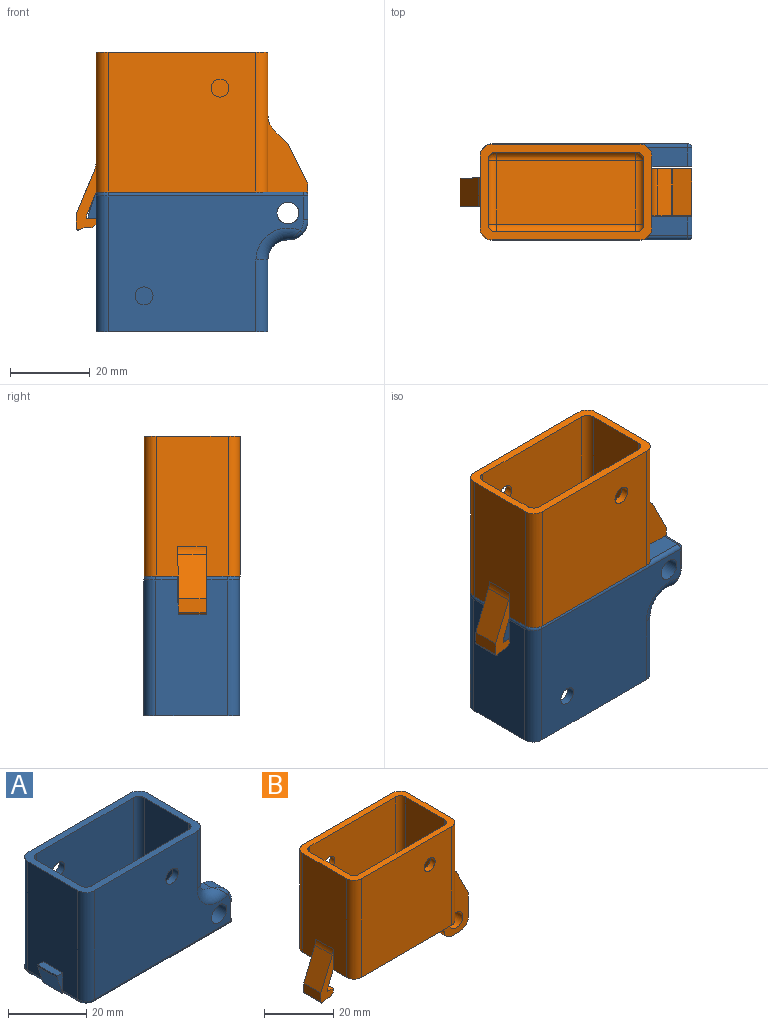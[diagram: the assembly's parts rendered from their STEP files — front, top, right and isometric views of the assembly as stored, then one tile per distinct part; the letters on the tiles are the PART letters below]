
ASSEMBLY  parts=2 mates=1
PART A: 62 faces, bbox 55.4x24.5x35 mm
  f0: plane 34x18mm, normal (-1,0,0), area 573.1mm2, adj f2,f37,f38,f39,f46,f47,f54,f61
  f1: plane 35x18mm, normal (1,0,0), area 536.5mm2, adj f2,f5,f15,f17,f22,f24,f42,f44
  f2: plane 43x24mm, normal (0,0,1), area 247.7mm2, adj f0,f1,f3,f4,f6,f7,f8,f9
  f3: plane 49x34mm, normal (0,1,0), area 1328.5mm2, adj f2,f19,f27,f42,f43,f46,f49,f50
  f4: plane 49x34mm, normal (0,-1,0), area 1328.5mm2, adj f2,f20,f28,f44,f45,f47,f56,f57
  f5: plane 52x22mm, normal (0,0,-1), area 1014.8mm2, adj f1,f15,f17,f25,f26,f37,f39,f41
  f6: plane 35x31mm, normal (0,-1,0), area 1069.1mm2, adj f2,f12,f14,f27,f31
  f7: plane 31x16mm, normal (1,0,0), area 496mm2, adj f2,f13,f14,f30
  f8: plane 35x31mm, normal (0,1,0), area 1069.1mm2, adj f2,f11,f13,f28,f34
  f9: plane 31x16mm, normal (-1,0,0), area 496mm2, adj f2,f11,f12,f35
  f10: plane 35x16mm, normal (0,0,1), area 560mm2, adj f30,f31,f34,f35
  f11: cylinder r=2mm len=31mm, axis (0,0,-1), area 97.4mm2, adj f2,f8,f9,f36
  f12: cylinder r=2mm len=31mm, axis (0,0,1), area 97.4mm2, adj f2,f6,f9,f33
  f13: cylinder r=2mm len=31mm, axis (0,0,1), area 97.4mm2, adj f2,f7,f8,f32
  f14: cylinder r=2mm len=31mm, axis (0,0,-1), area 97.4mm2, adj f2,f6,f7,f29
  f15: plane 17x10mm, normal (0,1,0), area 96mm2, adj f1,f5,f16,f20,f21,f22,f25
  f16: plane 6x4.75mm, normal (1,0,0), area 28.5mm2, adj f15,f21,f25,f57
  f17: plane 17x10mm, normal (0,-1,0), area 96mm2, adj f1,f5,f18,f19,f23,f24,f26
  f18: plane 6x4.75mm, normal (1,0,0), area 28.5mm2, adj f17,f23,f26,f50
  f19: cylinder r=2.75mm len=5.75mm, axis (0,1,0), area 99.4mm2, adj f3,f17
  f20: cylinder r=2.75mm len=5.75mm, axis (0,1,0), area 99.4mm2, adj f4,f15
  f21: cylinder r=5mm len=5mm, axis (0,1,0), area 34.2mm2, adj f15,f16,f22,f55,f56
  f22: cylinder r=5mm len=5mm, axis (0,-1,0), area 21.6mm2, adj f1,f15,f21,f45
  f23: cylinder r=5mm len=5mm, axis (0,1,0), area 34.2mm2, adj f17,f18,f24,f48,f49
  f24: cylinder r=5mm len=5mm, axis (0,-1,0), area 21.6mm2, adj f1,f17,f23,f43
  f25: cylinder r=1mm len=4.75mm, axis (0,1,0), area 7.5mm2, adj f5,f15,f16,f58
  f26: cylinder r=1mm len=4.75mm, axis (0,1,0), area 7.5mm2, adj f5,f17,f18,f51
  f27: cylinder r=2.25mm len=4.5mm, axis (0,1,0), area 28.3mm2, adj f3,f6
  f28: cylinder r=2.25mm len=4.5mm, axis (0,-1,0), area 28.3mm2, adj f4,f8
  f29: sphere r=2mm, area 6.3mm2, adj f14,f30,f31
  f30: cylinder r=2mm len=16mm, axis (0,1,0), area 50.3mm2, adj f7,f10,f29,f32
  f31: cylinder r=2mm len=35mm, axis (1,0,0), area 110mm2, adj f6,f10,f29,f33
  f32: sphere r=2mm, area 6.3mm2, adj f13,f30,f34
  f33: sphere r=2mm, area 6.3mm2, adj f12,f31,f35
  f34: cylinder r=2mm len=35mm, axis (-1,0,0), area 110mm2, adj f8,f10,f32,f36
  f35: cylinder r=2mm len=16mm, axis (0,-1,0), area 50.3mm2, adj f9,f10,f33,f36
  f36: sphere r=2mm, area 6.3mm2, adj f11,f34,f35
  f37: plane 6.56x3mm, normal (0,-1,0), area 7.3mm2, adj f0,f5,f38,f40,f41,f61
  f38: plane 7x2mm, normal (0,0,1), area 14mm2, adj f0,f37,f39,f40
  f39: plane 6.56x3mm, normal (0,1,0), area 7.3mm2, adj f0,f5,f38,f40,f41,f54
  f40: plane 7x0.56mm, normal (-1,0,0), area 3.9mm2, adj f37,f38,f39,f41
  f41: plane 7x6mm, normal (-0.95,0,-0.32), area 44.3mm2, adj f5,f37,f39,f40
  f42: cylinder r=3mm len=18mm, axis (0,0,-1), area 84.8mm2, adj f1,f2,f3,f43
  f43: torus R=8mm, axis (0,1,0), area 52.3mm2, adj f3,f24,f42,f48
  f44: cylinder r=3mm len=18mm, axis (0,0,1), area 84.8mm2, adj f1,f2,f4,f45
  f45: torus R=8mm, axis (0,1,0), area 52.3mm2, adj f4,f22,f44,f55
  f46: cylinder r=3mm len=34mm, axis (0,0,1), area 160.2mm2, adj f0,f2,f3,f53
  f47: cylinder r=3mm len=34mm, axis (0,0,-1), area 160.2mm2, adj f0,f2,f4,f60
  f48: bspline ~3.8x3mm, area 4.6mm2, adj f23,f43,f49
  f49: torus R=4mm, axis (0,1,0), area 5.2mm2, adj f3,f23,f48,f50
  f50: cylinder r=1mm len=6mm, axis (0,0,-1), area 9.4mm2, adj f3,f18,f49,f51
  f51: sphere r=1mm, area 1.6mm2, adj f26,f50,f52
  f52: cylinder r=1mm len=49mm, axis (-1,0,0), area 77mm2, adj f3,f5,f51,f53
  f53: torus R=2mm, axis (0,0,1), area 6.5mm2, adj f5,f46,f52,f54
  f54: cylinder r=1mm len=5.5mm, axis (0,-1,0), area 8.6mm2, adj f0,f5,f39,f53
  f55: bspline ~3.8x3mm, area 4.6mm2, adj f21,f45,f56
  f56: torus R=4mm, axis (0,1,0), area 5.2mm2, adj f4,f21,f55,f57
  f57: cylinder r=1mm len=6mm, axis (0,0,1), area 9.4mm2, adj f4,f16,f56,f58
  f58: sphere r=1mm, area 1.6mm2, adj f25,f57,f59
  f59: cylinder r=1mm len=49mm, axis (1,0,0), area 77mm2, adj f4,f5,f58,f60
  f60: torus R=2mm, axis (0,0,1), area 6.5mm2, adj f5,f47,f59,f61
  f61: cylinder r=1mm len=5.5mm, axis (0,-1,0), area 8.6mm2, adj f0,f5,f37,f60
PART B: 56 faces, bbox 58x24x45 mm
  f0: plane 7x1.34mm, normal (1,0,0), area 9.4mm2, adj f43,f46,f48,f52
  f1: plane 35x18mm, normal (-1,0,0), area 578.5mm2, adj f2,f4,f21,f22,f43,f44,f53
  f2: plane 43x24mm, normal (0,0,-1), area 1024.3mm2, adj f1,f3,f5,f6,f21,f22,f23,f24
  f3: plane 35x18mm, normal (1,0,0), area 405.9mm2, adj f2,f4,f16,f17,f23,f24,f42
  f4: plane 43x24mm, normal (0,0,1), area 247.7mm2, adj f1,f3,f5,f6,f7,f8,f9,f10
  f5: plane 37x35mm, normal (0,1,0), area 1279.1mm2, adj f2,f4,f20,f21,f24
  f6: plane 37x35mm, normal (0,-1,0), area 1279.1mm2, adj f2,f4,f19,f22,f23
  f7: plane 35x31mm, normal (0,-1,0), area 1069.1mm2, adj f4,f13,f15,f20,f27
  f8: plane 31x16mm, normal (1,0,0), area 496mm2, adj f4,f14,f15,f26
  f9: plane 35x31mm, normal (0,1,0), area 1069.1mm2, adj f4,f12,f14,f19,f30
  f10: plane 31x16mm, normal (-1,0,0), area 496mm2, adj f4,f12,f13,f31
  f11: plane 35x16mm, normal (0,0,1), area 560mm2, adj f26,f27,f30,f31
  f12: cylinder r=2mm len=31mm, axis (0,0,-1), area 97.4mm2, adj f4,f9,f10,f32
  f13: cylinder r=2mm len=31mm, axis (0,0,1), area 97.4mm2, adj f4,f7,f10,f29
  f14: cylinder r=2mm len=31mm, axis (0,0,1), area 97.4mm2, adj f4,f8,f9,f28
  f15: cylinder r=2mm len=31mm, axis (0,0,-1), area 97.4mm2, adj f4,f7,f8,f25
  f16: plane 29.07x10mm, normal (0,-1,0), area 179mm2, adj f3,f18,f33,f34,f35,f36,f37,f38
  f17: plane 29.07x10mm, normal (0,1,0), area 179mm2, adj f3,f18,f33,f34,f35,f36,f37,f38
  f18: plane 11.75x2mm, normal (1,0,0), area 23.5mm2, adj f16,f17,f34,f40
  f19: cylinder r=2.25mm len=4.5mm, axis (0,-1,0), area 28.3mm2, adj f6,f9
  f20: cylinder r=2.25mm len=4.5mm, axis (0,1,0), area 28.3mm2, adj f5,f7
  f21: cylinder r=3mm len=35mm, axis (0,0,1), area 164.9mm2, adj f1,f2,f4,f5
  f22: cylinder r=3mm len=35mm, axis (0,0,-1), area 164.9mm2, adj f1,f2,f4,f6
  f23: cylinder r=3mm len=35mm, axis (0,0,1), area 164.9mm2, adj f2,f3,f4,f6
  f24: cylinder r=3mm len=35mm, axis (0,0,-1), area 164.9mm2, adj f2,f3,f4,f5
  f25: sphere r=2mm, area 6.3mm2, adj f15,f26,f27
  f26: cylinder r=2mm len=16mm, axis (0,1,0), area 50.3mm2, adj f8,f11,f25,f28
  f27: cylinder r=2mm len=35mm, axis (1,0,0), area 110mm2, adj f7,f11,f25,f29
  f28: sphere r=2mm, area 6.3mm2, adj f14,f26,f30
  f29: sphere r=2mm, area 6.3mm2, adj f13,f27,f31
  f30: cylinder r=2mm len=35mm, axis (-1,0,0), area 110mm2, adj f9,f11,f28,f32
  f31: cylinder r=2mm len=16mm, axis (0,-1,0), area 50.3mm2, adj f10,f11,f29,f32
  f32: sphere r=2mm, area 6.3mm2, adj f12,f30,f31
  f33: plane 11.75x6.5mm, normal (-1,0,0), area 76.4mm2, adj f2,f16,f17,f37
  f34: plane 11.75x6.5mm, normal (1,0,0), area 76.4mm2, adj f16,f17,f18,f38
  f35: plane 11.75x3mm, normal (0,0,-1), area 35.2mm2, adj f16,f17,f37,f38
  f36: cylinder r=2.75mm len=11.75mm, axis (0,1,0), area 203mm2, adj f16,f17
  f37: cylinder r=3.5mm len=11.75mm, axis (0,-1,0), area 64.6mm2, adj f16,f17,f33,f35
  f38: cylinder r=3.5mm len=11.75mm, axis (0,1,0), area 64.6mm2, adj f16,f17,f34,f35
  f39: plane 11.75x3.42mm, normal (0.71,0,0.71), area 56.8mm2, adj f16,f17,f41,f42
  f40: plane 11.75x9.86mm, normal (0.89,0,0.45), area 129.5mm2, adj f16,f17,f18,f41
  f41: cylinder r=1mm len=11.75mm, axis (0,1,0), area 3.8mm2, adj f16,f17,f39,f40
  f42: cylinder r=5mm len=11.75mm, axis (0,-1,0), area 46.1mm2, adj f3,f16,f17,f39
  f43: plane 16.8x5mm, normal (0,-1,0), area 38mm2, adj f0,f1,f45,f47,f48,f49,f50,f51
  f44: plane 7.27x2.61mm, normal (0,1,-0.02), area 8.3mm2, adj f1,f46,f51,f53
  f45: plane 7x3.3mm, normal (-1,0,0), area 23.1mm2, adj f43,f46,f51,f55
  f46: plane 9.53x5mm, normal (0,1,0), area 29.7mm2, adj f0,f44,f45,f47,f48,f49,f50,f51
  f47: plane 7x2mm, normal (0,0,-1), area 14mm2, adj f43,f46,f52,f54
  f48: plane 7x2.26mm, normal (0,0,1), area 15.8mm2, adj f0,f43,f46,f50
  f49: plane 7x5.75mm, normal (0.93,0,-0.37), area 43.2mm2, adj f2,f43,f46,f50
  f50: plane 7x0.91mm, normal (1,0,0), area 6.4mm2, adj f43,f46,f48,f49
  f51: plane 11.08x7.13mm, normal (-0.92,0,0.38), area 84.4mm2, adj f43,f44,f45,f46,f53
  f52: plane 7x1mm, normal (0.71,0,-0.71), area 9.9mm2, adj f0,f43,f46,f47
  f53: cylinder r=5mm len=7.18mm, axis (0,1,0), area 14.1mm2, adj f1,f43,f44,f51
  f54: plane 7x1.33mm, normal (0.35,0,-0.94), area 9.9mm2, adj f43,f46,f47,f55
  f55: cylinder r=0.5mm len=7mm, axis (0,1,0), area 6.7mm2, adj f43,f45,f46,f54
PLACE A rot(axis=(-1,0,0),180deg) t=(-23.22,-24.93,-11.77)mm
PLACE B t=(-23.22,-21.04,-11.77)mm
MATE revolute A.f19 <-> B.f36  axis (0,-1,0) through (8.12,-32.04,-17.02)mm
